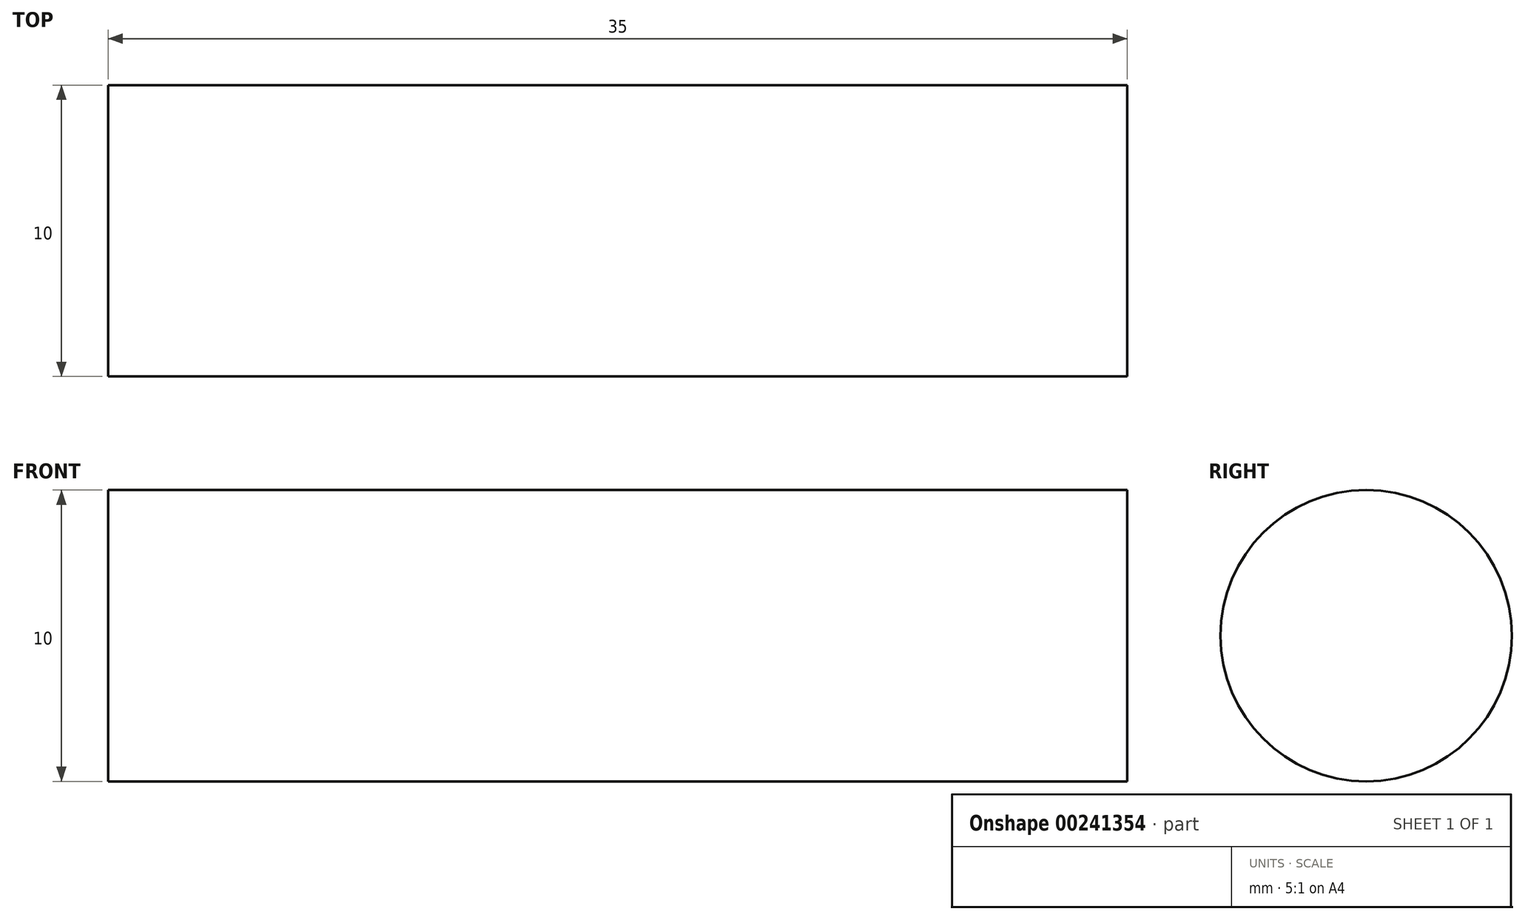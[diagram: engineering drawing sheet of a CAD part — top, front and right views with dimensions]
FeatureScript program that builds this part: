
annotation { "Feature Type Name" : "Feature", "Feature Type Description" : "" }
export const myFeature = defineFeature(function(context is Context, id is Id, definition is map)
    precondition{}
    {
        {
            var Q0;
            Q0=qCreatedBy(makeId("Right.planeOp"),FACE);
            var sketch = newSketch(context, id + "F0", { "sketchPlane" : qUnion([Q0])});
            skCircle(sketch, "E0", {"center": v(0, 0) * mm, "radius": 5 * mm});
            skSolve(sketch);
        }
        {
            var Q0;
            Q0 = qSketchRegion(id + "F0", true);
            extrude(context, id + "F1", {"entities" : qUnion([Q0]), "depth" : 35 * mm});
        }
    });
